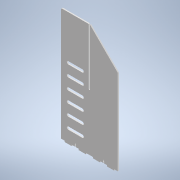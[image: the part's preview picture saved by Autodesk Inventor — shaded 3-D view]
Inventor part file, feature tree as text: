
AUTODESK INVENTOR PART (.ipt)
format: ipt  version: 2021.1 (Build 251245010, 245A)  size: 226,816 bytes
history: native  units: mm
features: other x4, extrude x2, sketch x2, reference x2
ambient origin geometry x8: Origin, YZ Plane, XZ Plane, XY Plane, X Axis, Y Axis, Z Axis, Center Point
bodies: Body1 (feature_tree)
feature tree (10):
  other  "Твердое тело1"
  extrude  "Корпус"  Depth=6.2mm
  extrude  "Пазы"  Depth=300.0mm
  sketch  "Эскиз1"
  sketch  "Эскиз2"
  reference  "Ссылка1"
  reference  "Ссылка2"
  other  "<userpath>\Documents\Savka\3d\Korp.iam"
  other  "Korp.iam"
  other  "Korpus 2:1"
